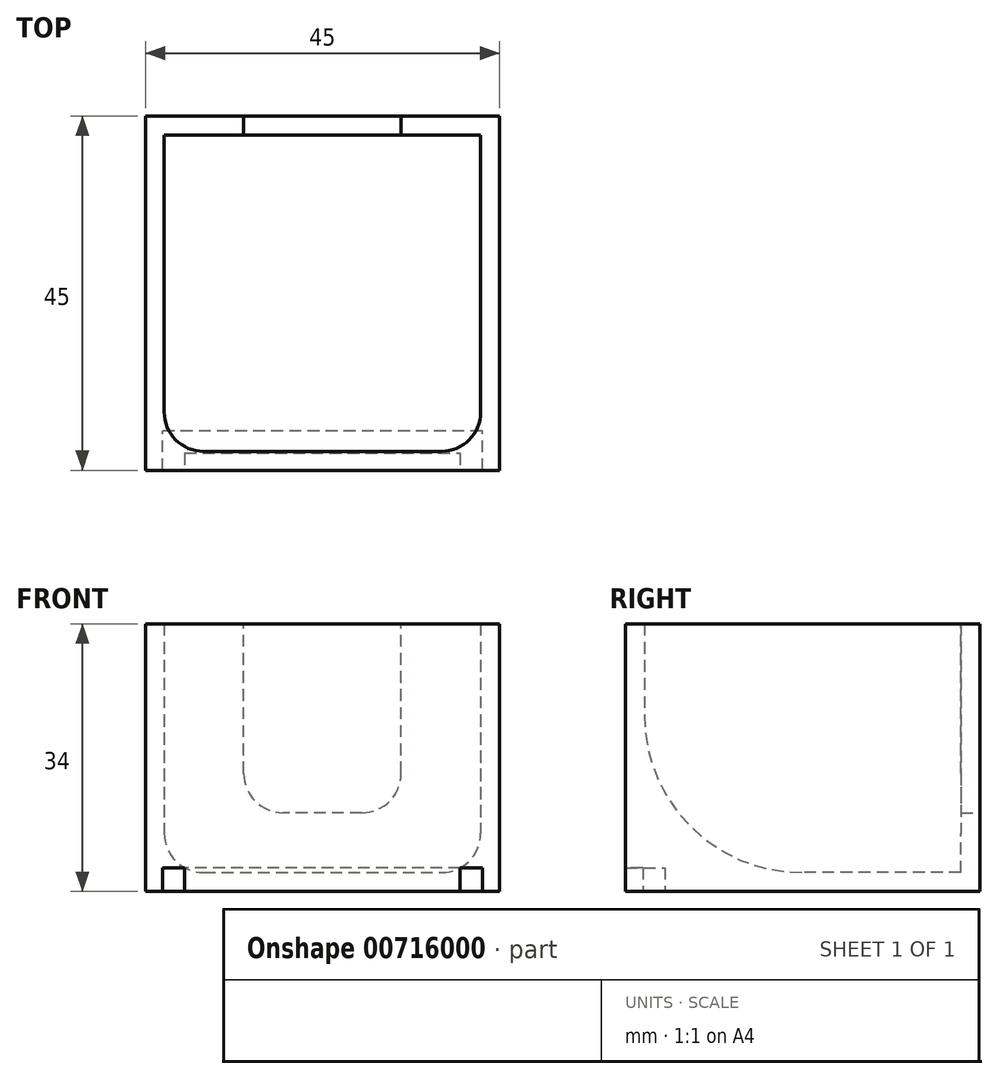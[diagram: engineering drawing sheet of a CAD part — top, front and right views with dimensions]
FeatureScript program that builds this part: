
annotation { "Feature Type Name" : "Feature", "Feature Type Description" : "" }
export const myFeature = defineFeature(function(context is Context, id is Id, definition is map)
    precondition{}
    {
        {
            var Q0;
            Q0=qCreatedBy(makeId("Top.planeOp"),FACE);
            var sketch = newSketch(context, id + "F0", { "sketchPlane" : qUnion([Q0])});
            skLineSegment(sketch, "E0.bottom", {"start": v(-22.5, 22.5) * mm, "end": v(22.5, 22.5) * mm});
            skLineSegment(sketch, "E0.top", {"start": v(-22.5, -22.5) * mm, "end": v(22.5, -22.5) * mm});
            skLineSegment(sketch, "E0.left", {"start": v(-22.5, 22.5) * mm, "end": v(-22.5, -22.5) * mm});
            skLineSegment(sketch, "E0.right", {"start": v(22.5, 22.5) * mm, "end": v(22.5, -22.5) * mm});
            skPoint(sketch, "E0.middle", {"position": v(0, 0) * mm});
            skSolve(sketch);
        }
        {
            var Q0;
            Q0=makeQuery(id+"F0.imprint","IMPRINT",FACE,{"disambiguationData":[TD([[makeQuery(id+"F0.imprint","IMPRINT",EDGE,{"derivedFrom":sQuery(id+"F0.wireOp",EDGE,"E0.bottom")}),-1.0]])]});
            extrude(context, id + "F1", {"entities" : qUnion([Q0]), "depth" : 34 * mm, "offsetDistance" : 25 * mm});
        }
        {
            var Q0;
            Q0=makeQuery(id+"F1.opExtrude","CAP_FACE",FACE,{"disambiguationData":[OSD([sQuery(id+"F0.wireOp",EDGE,"E0.bottom"),sQuery(id+"F0.wireOp",EDGE,"E0.top"),sQuery(id+"F0.wireOp",EDGE,"E0.left"),sQuery(id+"F0.wireOp",EDGE,"E0.right")])],"isStart":false});
            shell(context, id + "F2", {"entities" : qUnion([Q0]), "thickness" : 2.4 * mm});
        }
        {
            var Q0;
            {var subQ0=sQuery(id+"F0.wireOp",EDGE,"E0.top");Q0=makeQuery(id+"F2.opShell","OFFSET_EDGE",EDGE,{"disambiguationData":[OSD([subQ0]),TDD([makeQuery(id+"F1.opExtrude","CAP_EDGE",EDGE,{"disambiguationData":[OSD([subQ0])],"isStart":true})])]});}
            fillet(context, id + "F3", {"entities" : qUnion([Q0]), "radius" : 20 * mm, "tangentPropagation" : true, "allowEdgeOverflow" : false});
        }
        {
            var Q0;
            {var subQ0=sQuery(id+"F0.wireOp",EDGE,"E0.left");Q0=makeQuery(id+"F2.opShell","OFFSET_EDGE",EDGE,{"disambiguationData":[OSD([subQ0]),TDD([makeQuery(id+"F1.opExtrude","CAP_EDGE",EDGE,{"disambiguationData":[OSD([subQ0])],"isStart":true})])]});}
            var Q1;
            {var subQ0=sQuery(id+"F0.wireOp",EDGE,"E0.right");Q1=makeQuery(id+"F2.opShell","OFFSET_EDGE",EDGE,{"disambiguationData":[OSD([subQ0]),TDD([makeQuery(id+"F1.opExtrude","CAP_EDGE",EDGE,{"disambiguationData":[OSD([subQ0])],"isStart":true})])]});}
            fillet(context, id + "F4", {"entities" : qUnion([Q0, Q1]), "radius" : 5 * mm, "tangentPropagation" : true, "allowEdgeOverflow" : false});
        }
        {
            var Q0;
            Q0=makeQuery(id+"F1.opExtrude","SWEPT_FACE",FACE,{"disambiguationData":[OSD([sQuery(id+"F0.wireOp",EDGE,"E0.bottom")])]});
            var sketch = newSketch(context, id + "F5", { "sketchPlane" : qUnion([Q0])});
            skPoint(sketch, "E1", {"position": v(-22.5, 34) * mm});
            skPoint(sketch, "E2", {"position": v(22.5, 34) * mm});
            skPoint(sketch, "E3", {"position": v(0, 34) * mm});
            skPoint(sketch, "E4", {"position": v(0, 0) * mm});
            skLineSegment(sketch, "E5.bottom", {"start": v(-10, 10) * mm, "end": v(10, 10) * mm});
            skLineSegment(sketch, "E5.top", {"start": v(-10, 58) * mm, "end": v(10, 58) * mm});
            skLineSegment(sketch, "E5.left", {"start": v(-10, 10) * mm, "end": v(-10, 58) * mm});
            skLineSegment(sketch, "E5.right", {"start": v(10, 10) * mm, "end": v(10, 58) * mm});
            skSolve(sketch);
        }
        {
            var Q0;
            {var subQ0=sQuery(id+"F5.wireOp",EDGE,"E5.bottom");Q0=makeQuery(id+"F5.imprint","IMPRINT",FACE,{"disambiguationData":[TD([[makeQuery(id+"F5.imprint","IMPRINT",EDGE,{"derivedFrom":subQ0}),1.0]])]});}
            extrude(context, id + "F6", {"entities" : qUnion([Q0]), "operationType" : NewBodyOperationType.REMOVE, "oppositeDirection" : true, "depth" : 5 * mm, "offsetDistance" : 25 * mm});
        }
        {
            var Q0;
            Q0=makeQuery(id+"F6.boolean.opBoolean","COPY",EDGE,{"derivedFrom":makeQuery(id+"F6.opExtrude","SWEPT_EDGE",EDGE,{"disambiguationData":[OSD([sQuery(id+"F5.wireOp",EDGE,"E5.bottom"),sQuery(id+"F5.wireOp",EDGE,"E5.left")])]})});
            var Q1;
            Q1=makeQuery(id+"F6.boolean.opBoolean","COPY",EDGE,{"derivedFrom":makeQuery(id+"F6.opExtrude","SWEPT_EDGE",EDGE,{"disambiguationData":[OSD([sQuery(id+"F5.wireOp",EDGE,"E5.bottom"),sQuery(id+"F5.wireOp",EDGE,"E5.right")])]})});
            fillet(context, id + "F7", {"entities" : qUnion([Q0, Q1]), "radius" : 5 * mm, "tangentPropagation" : true, "allowEdgeOverflow" : false});
        }
        {
            var Q0;
            Q0=makeQuery(id+"F1.opExtrude","CAP_FACE",FACE,{"disambiguationData":[OSD([sQuery(id+"F0.wireOp",EDGE,"E0.bottom"),sQuery(id+"F0.wireOp",EDGE,"E0.top"),sQuery(id+"F0.wireOp",EDGE,"E0.left"),sQuery(id+"F0.wireOp",EDGE,"E0.right")])],"isStart":true});
            var sketch = newSketch(context, id + "F8", { "sketchPlane" : qUnion([Q0])});
            skPoint(sketch, "E6", {"position": v(-22.5, 20.3) * mm});
            skLineSegment(sketch, "E7", {"start": v(-22.5, 20.3) * mm, "end": v(-20.3, 20.3) * mm, "construction": true});
            skLineSegment(sketch, "E8", {"start": v(22.5, 20.3) * mm, "end": v(22.5, 17.5) * mm, "construction": true});
            skLineSegment(sketch, "E9", {"start": v(22.5, 17.5) * mm, "end": v(20.3, 17.5) * mm, "construction": true});
            skLineSegment(sketch, "E10", {"start": v(-22.5, 17.5) * mm, "end": v(-22.5, 20.3) * mm, "construction": true});
            skPoint(sketch, "E11", {"position": v(-20.3, 22.5) * mm});
            skPoint(sketch, "E12", {"position": v(20.3, 22.5) * mm});
            skLineSegment(sketch, "E13", {"start": v(-20.3, 22.5) * mm, "end": v(-20.3, 20) * mm});
            skLineSegment(sketch, "E14", {"start": v(20.3, 22.5) * mm, "end": v(20.3, 20) * mm});
            skPoint(sketch, "E15", {"position": v(-20.3, 20) * mm});
            skPoint(sketch, "E16", {"position": v(20.3, 20) * mm});
            skLineSegment(sketch, "E17", {"start": v(-20.3, 20) * mm, "end": v(-20.3, 17.5) * mm});
            skLineSegment(sketch, "E18", {"start": v(-20.3, 20.3) * mm, "end": v(-17.5, 20.3) * mm, "construction": true});
            skLineSegment(sketch, "E19", {"start": v(-20.3, 17.5) * mm, "end": v(-22.5, 17.5) * mm, "construction": true});
            skLineSegment(sketch, "E20", {"start": v(20.3, 17.5) * mm, "end": v(-20.3, 17.5) * mm});
            skLineSegment(sketch, "E21", {"start": v(20.3, 20) * mm, "end": v(20.3, 17.5) * mm});
            skLineSegment(sketch, "E22", {"start": v(20.3, 20.3) * mm, "end": v(22.5, 20.3) * mm, "construction": true});
            skLineSegment(sketch, "E23", {"start": v(-17.5, 20.3) * mm, "end": v(-17.5, 22.5) * mm});
            skLineSegment(sketch, "E24", {"start": v(17.5, 20.3) * mm, "end": v(17.5, 22.5) * mm});
            skLineSegment(sketch, "E25", {"start": v(-20.3, 22.5) * mm, "end": v(-17.5, 22.5) * mm});
            skLineSegment(sketch, "E26", {"start": v(17.5, 22.5) * mm, "end": v(20.3, 22.5) * mm});
            skLineSegment(sketch, "E27", {"start": v(-17.5, 20.3) * mm, "end": v(17.5, 20.3) * mm});
            skLineSegment(sketch, "E28", {"start": v(17.5, 20.3) * mm, "end": v(20.3, 20.3) * mm, "construction": true});
            skSolve(sketch);
        }
        {
            var Q0;
            Q0=makeQuery(id+"F8.imprint","IMPRINT",FACE,{"disambiguationData":[TD([[makeQuery(id+"F8.imprint","IMPRINT",EDGE,{"derivedFrom":sQuery(id+"F8.wireOp",EDGE,"E17")}),1.0]])]});
            extrude(context, id + "F9", {"entities" : qUnion([Q0]), "operationType" : NewBodyOperationType.REMOVE, "oppositeDirection" : true, "depth" : 3 * mm, "offsetDistance" : 25 * mm});
        }
    });
